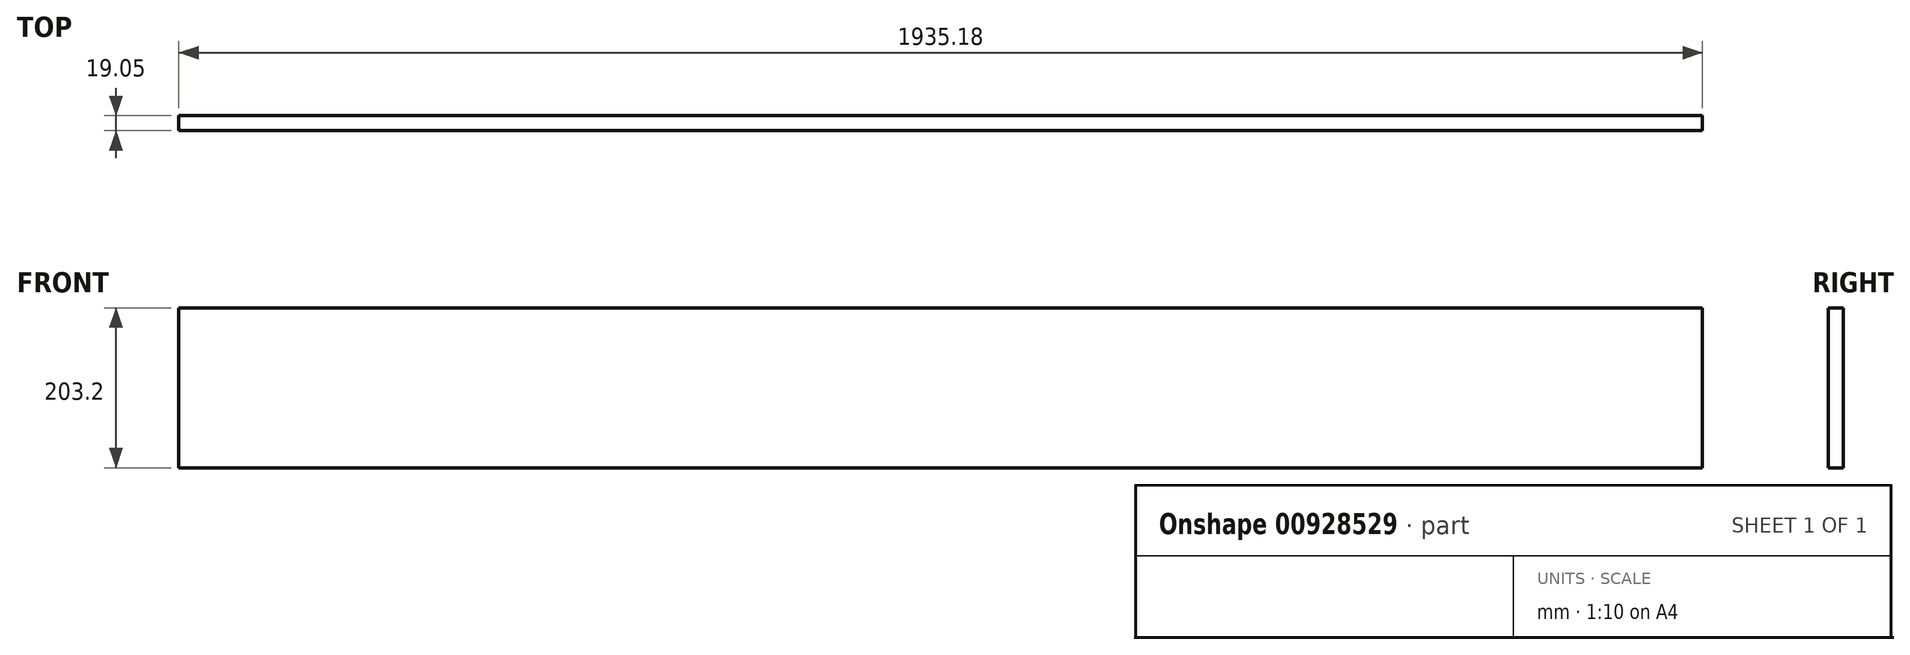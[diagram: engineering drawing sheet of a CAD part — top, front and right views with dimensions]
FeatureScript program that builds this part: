
annotation { "Feature Type Name" : "Feature", "Feature Type Description" : "" }
export const myFeature = defineFeature(function(context is Context, id is Id, definition is map)
    precondition{}
    {
        {
            var Q0;
            Q0=qCreatedBy(makeId("Front.planeOp"),FACE);
            var sketch = newSketch(context, id + "F0", { "sketchPlane" : qUnion([Q0])});
            skLineSegment(sketch, "E0.bottom", {"start": v(-967.59, 101.6) * mm, "end": v(967.59, 101.6) * mm});
            skLineSegment(sketch, "E0.top", {"start": v(-967.59, -101.6) * mm, "end": v(967.59, -101.6) * mm});
            skLineSegment(sketch, "E0.left", {"start": v(-967.59, 101.6) * mm, "end": v(-967.59, -101.6) * mm});
            skLineSegment(sketch, "E0.right", {"start": v(967.59, 101.6) * mm, "end": v(967.59, -101.6) * mm});
            skPoint(sketch, "E0.middle", {"position": v(0, 0) * mm});
            skSolve(sketch);
        }
        {
            var Q0;
            Q0=makeQuery(id+"F0.imprint","IMPRINT",FACE,{"disambiguationData":[TD([[makeQuery(id+"F0.imprint","IMPRINT",EDGE,{"derivedFrom":sQuery(id+"F0.wireOp",EDGE,"E0.bottom")}),-1.0]])]});
            extrude(context, id + "F1", {"entities" : qUnion([Q0]), "depth" : 19.05 * mm, "offsetDistance" : 25.4 * mm});
        }
    });
